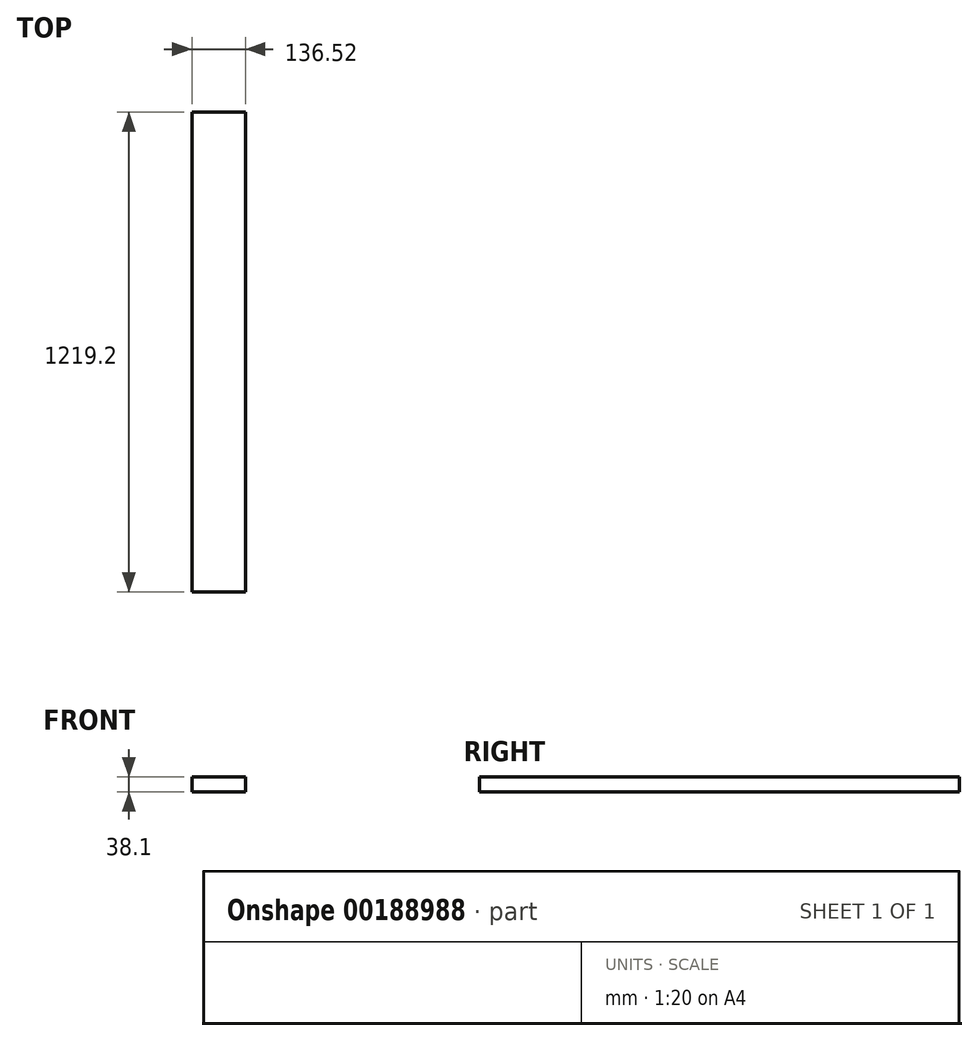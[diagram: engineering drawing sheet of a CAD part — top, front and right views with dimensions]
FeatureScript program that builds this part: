
annotation { "Feature Type Name" : "Feature", "Feature Type Description" : "" }
export const myFeature = defineFeature(function(context is Context, id is Id, definition is map)
    precondition{}
    {
        {
            var Q0;
            Q0=qCreatedBy(makeId("Front.planeOp"),FACE);
            var sketch = newSketch(context, id + "F0", { "sketchPlane" : qUnion([Q0])});
            skLineSegment(sketch, "E0.bottom", {"start": v(68.26, -19.05) * mm, "end": v(-68.26, -19.05) * mm});
            skLineSegment(sketch, "E0.top", {"start": v(68.26, 19.05) * mm, "end": v(-68.26, 19.05) * mm});
            skLineSegment(sketch, "E0.left", {"start": v(68.26, -19.05) * mm, "end": v(68.26, 19.05) * mm});
            skLineSegment(sketch, "E0.right", {"start": v(-68.26, -19.05) * mm, "end": v(-68.26, 19.05) * mm});
            skPoint(sketch, "E0.middle", {"position": v(0, 0) * mm});
            skSolve(sketch);
        }
        {
            var Q0;
            Q0 = qSketchRegion(id + "F0", true);
            extrude(context, id + "F1", {"entities" : qUnion([Q0]), "depth" : 1219.2 * mm});
        }
    });
